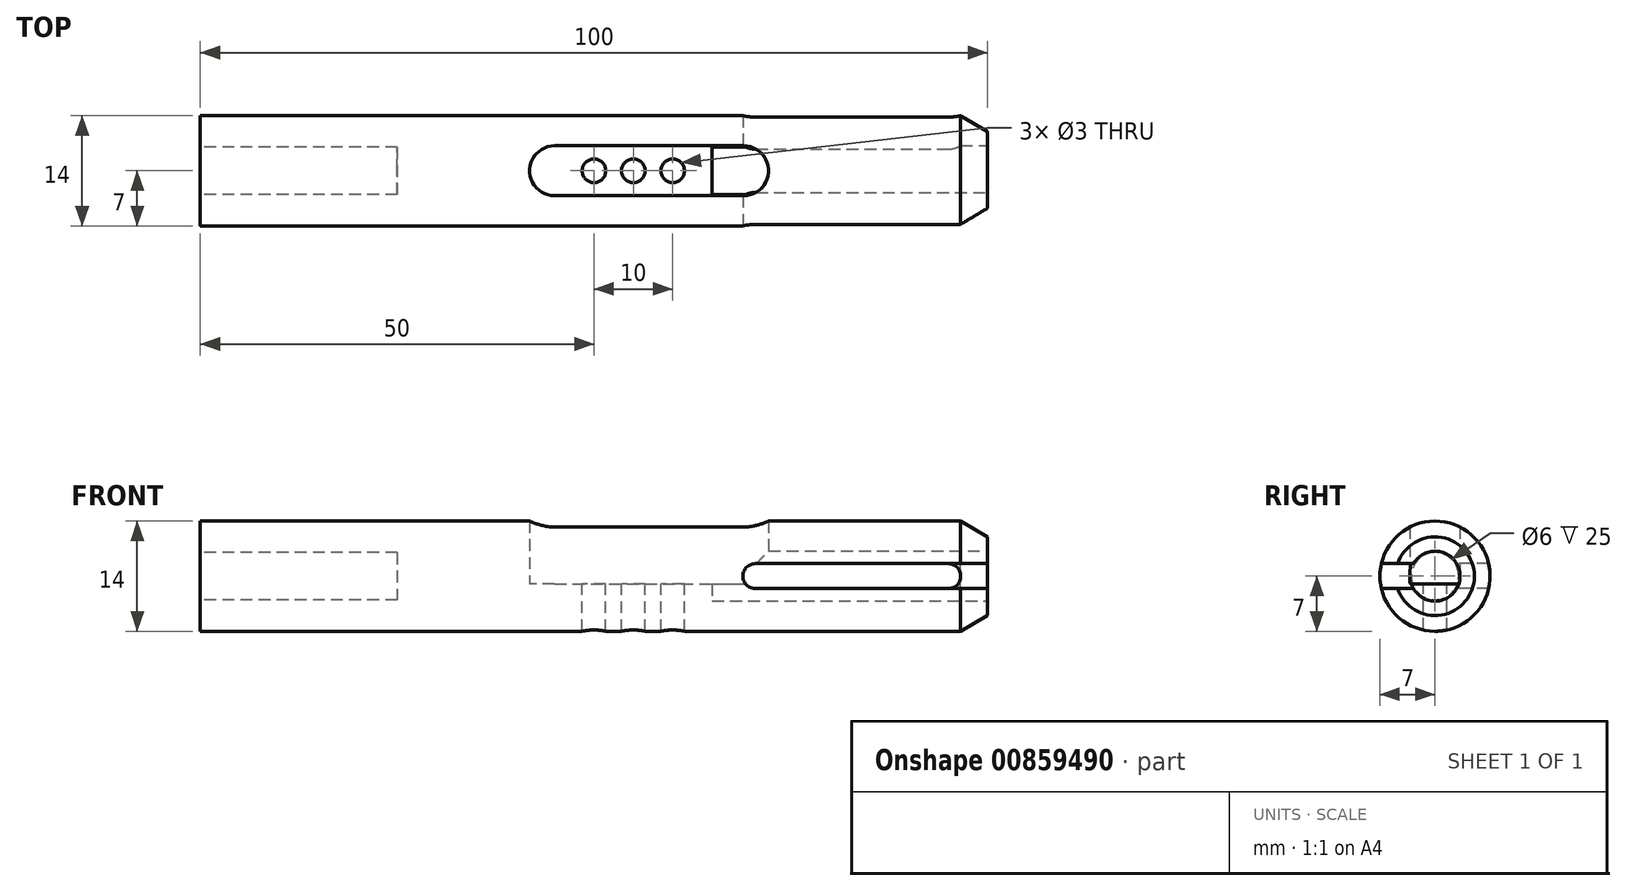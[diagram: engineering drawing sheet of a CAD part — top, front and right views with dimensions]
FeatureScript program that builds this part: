
annotation { "Feature Type Name" : "Feature", "Feature Type Description" : "" }
export const myFeature = defineFeature(function(context is Context, id is Id, definition is map)
    precondition{}
    {
        {
            var Q0;
            Q0=qCreatedBy(makeId("Right.planeOp"),FACE);
            var sketch = newSketch(context, id + "F0", { "sketchPlane" : qUnion([Q0])});
            skCircle(sketch, "E0", {"center": v(0, 0) * mm, "radius": 7 * mm});
            skSolve(sketch);
        }
        {
            var Q0;
            Q0=qSketchRegion(id+"F0",true);
            extrude(context, id + "F1", {"entities" : qUnion([Q0]), "depth" : 100 * mm, "offsetDistance" : 25 * mm});
        }
        {
            var Q0;
            Q0=makeQuery(id+"F1.opExtrude","CAP_FACE",FACE,{"disambiguationData":[OSD([sQuery(id+"F0.wireOp",EDGE,"E0")])],"isStart":false});
            var sketch = newSketch(context, id + "F2", { "sketchPlane" : qUnion([Q0])});
            skCircle(sketch, "E1", {"center": v(0, 0) * mm, "radius": 3.18 * mm});
            skSolve(sketch);
        }
        {
            var Q0;
            Q0=qSketchRegion(id+"F2",true);
            extrude(context, id + "F3", {"entities" : qUnion([Q0]), "operationType" : NewBodyOperationType.REMOVE, "oppositeDirection" : true, "depth" : 35 * mm, "offsetDistance" : 25 * mm});
        }
        {
            var Q0;
            Q0=makeQuery(id+"F1.opExtrude","CAP_FACE",FACE,{"disambiguationData":[OSD([sQuery(id+"F0.wireOp",EDGE,"E0")])],"isStart":true});
            var sketch = newSketch(context, id + "F4", { "sketchPlane" : qUnion([Q0])});
            skCircle(sketch, "E2", {"center": v(0, 0) * mm, "radius": 3 * mm});
            skSolve(sketch);
        }
        {
            var Q0;
            Q0=qSketchRegion(id+"F4",true);
            extrude(context, id + "F5", {"entities" : qUnion([Q0]), "operationType" : NewBodyOperationType.REMOVE, "oppositeDirection" : true, "depth" : 25 * mm, "offsetDistance" : 25 * mm});
        }
        {
            var Q0;
            Q0=makeQuery(id+"F1.opExtrude","CAP_EDGE",EDGE,{"disambiguationData":[OSD([sQuery(id+"F0.wireOp",EDGE,"E0")])],"isStart":false});
            chamfer(context, id + "F6", {"entities" : qUnion([Q0]), "chamferType" : ChamferType.OFFSET_ANGLE, "width" : 2 * mm, "oppositeDirection" : false, "angle" : 60 * degree});
        }
        {
            var Q0;
            Q0=qCreatedBy(makeId("Top.planeOp"),FACE);
            var sketch = newSketch(context, id + "F7", { "sketchPlane" : qUnion([Q0])});
            skArc(sketch, "E3", {"start": v(45, 3.17) * mm, "mid": v(41.83, 0) * mm, "end": v(45, -3.18) * mm});
            skArc(sketch, "E4", {"start": v(69, -3.18) * mm, "mid": v(72.17, 0) * mm, "end": v(69, 3.17) * mm});
            skLineSegment(sketch, "E5", {"start": v(45, 3.17) * mm, "end": v(69, 3.17) * mm});
            skLineSegment(sketch, "E6", {"start": v(45, -3.18) * mm, "end": v(69, -3.18) * mm});
            skLineSegment(sketch, "E7", {"start": v(69, -3.17) * mm, "end": v(45, -3.18) * mm});
            skSolve(sketch);
        }
        {
            var Q0;
            Q0=qSketchRegion(id+"F7",true);
            extrude(context, id + "F8", {"entities" : qUnion([Q0]), "operationType" : NewBodyOperationType.REMOVE, "endBound" : BoundingType.THROUGH_ALL, "depth" : 25 * mm, "offsetDistance" : 25 * mm, "hasSecondDirection" : true, "secondDirectionOppositeDirection" : true, "secondDirectionDepth" : 1 * mm});
        }
        {
            var Q0;
            Q0=qCreatedBy(makeId("Front.planeOp"),FACE);
            var sketch = newSketch(context, id + "F9", { "sketchPlane" : qUnion([Q0])});
            skArc(sketch, "E8", {"start": v(70.5, 1.59) * mm, "mid": v(68.91, 0) * mm, "end": v(70.5, -1.59) * mm});
            skArc(sketch, "E9", {"start": v(95, -1.59) * mm, "mid": v(96.59, 0) * mm, "end": v(95, 1.59) * mm});
            skLineSegment(sketch, "E10", {"start": v(70.5, 1.59) * mm, "end": v(95, 1.59) * mm});
            skLineSegment(sketch, "E11", {"start": v(70.5, -1.59) * mm, "end": v(95, -1.59) * mm});
            skSolve(sketch);
        }
        {
            var Q0;
            Q0=qSketchRegion(id+"F9",true);
            extrude(context, id + "F10", {"entities" : qUnion([Q0]), "operationType" : NewBodyOperationType.REMOVE, "endBound" : BoundingType.THROUGH_ALL, "oppositeDirection" : true, "depth" : 25 * mm, "offsetDistance" : 25 * mm, "hasSecondDirection" : true, "secondDirectionBound" : SecondDirectionBoundingType.THROUGH_ALL, "secondDirectionOppositeDirection" : false, "secondDirectionDepth" : 25 * mm});
        }
        {
            var Q0;
            Q0=qCreatedBy(makeId("Front.planeOp"),FACE);
            var sketch = newSketch(context, id + "F11", { "sketchPlane" : qUnion([Q0])});
            skLineSegment(sketch, "E12.bottom", {"start": v(88, 1.59) * mm, "end": v(103, 1.59) * mm});
            skLineSegment(sketch, "E12.top", {"start": v(88, -1.59) * mm, "end": v(103, -1.59) * mm});
            skLineSegment(sketch, "E12.left", {"start": v(88, 1.59) * mm, "end": v(88, -1.59) * mm});
            skLineSegment(sketch, "E12.right", {"start": v(103, 1.59) * mm, "end": v(103, -1.59) * mm});
            skSolve(sketch);
        }
        {
            var Q0;
            Q0=qSketchRegion(id+"F11",true);
            extrude(context, id + "F12", {"entities" : qUnion([Q0]), "operationType" : NewBodyOperationType.REMOVE, "depth" : 25 * mm, "offsetDistance" : 25 * mm});
        }
        {
            var Q0;
            Q0=makeQuery(id+"F8.boolean.opBoolean","COPY",FACE,{"derivedFrom":makeQuery(id+"F8.opExtrude","CAP_FACE",FACE,{"disambiguationData":[OSD([sQuery(id+"F7.wireOp",EDGE,"E3"),sQuery(id+"F7.wireOp",EDGE,"E4"),sQuery(id+"F7.wireOp",EDGE,"E5"),sQuery(id+"F7.wireOp",EDGE,"E7")])],"isStart":true})});
            var sketch = newSketch(context, id + "F13", { "sketchPlane" : qUnion([Q0])});
            skCircle(sketch, "E13", {"center": v(50, 0) * mm, "radius": 1.5 * mm});
            skCircle(sketch, "E14", {"center": v(55, 0) * mm, "radius": 1.5 * mm});
            skCircle(sketch, "E15", {"center": v(60, 0) * mm, "radius": 1.5 * mm});
            skSolve(sketch);
        }
        {
            var Q0;
            Q0=qSketchRegion(id+"F13",true);
            extrude(context, id + "F14", {"entities" : qUnion([Q0]), "operationType" : NewBodyOperationType.REMOVE, "endBound" : BoundingType.THROUGH_ALL, "oppositeDirection" : true, "depth" : 25 * mm, "offsetDistance" : 25 * mm});
        }
    });
